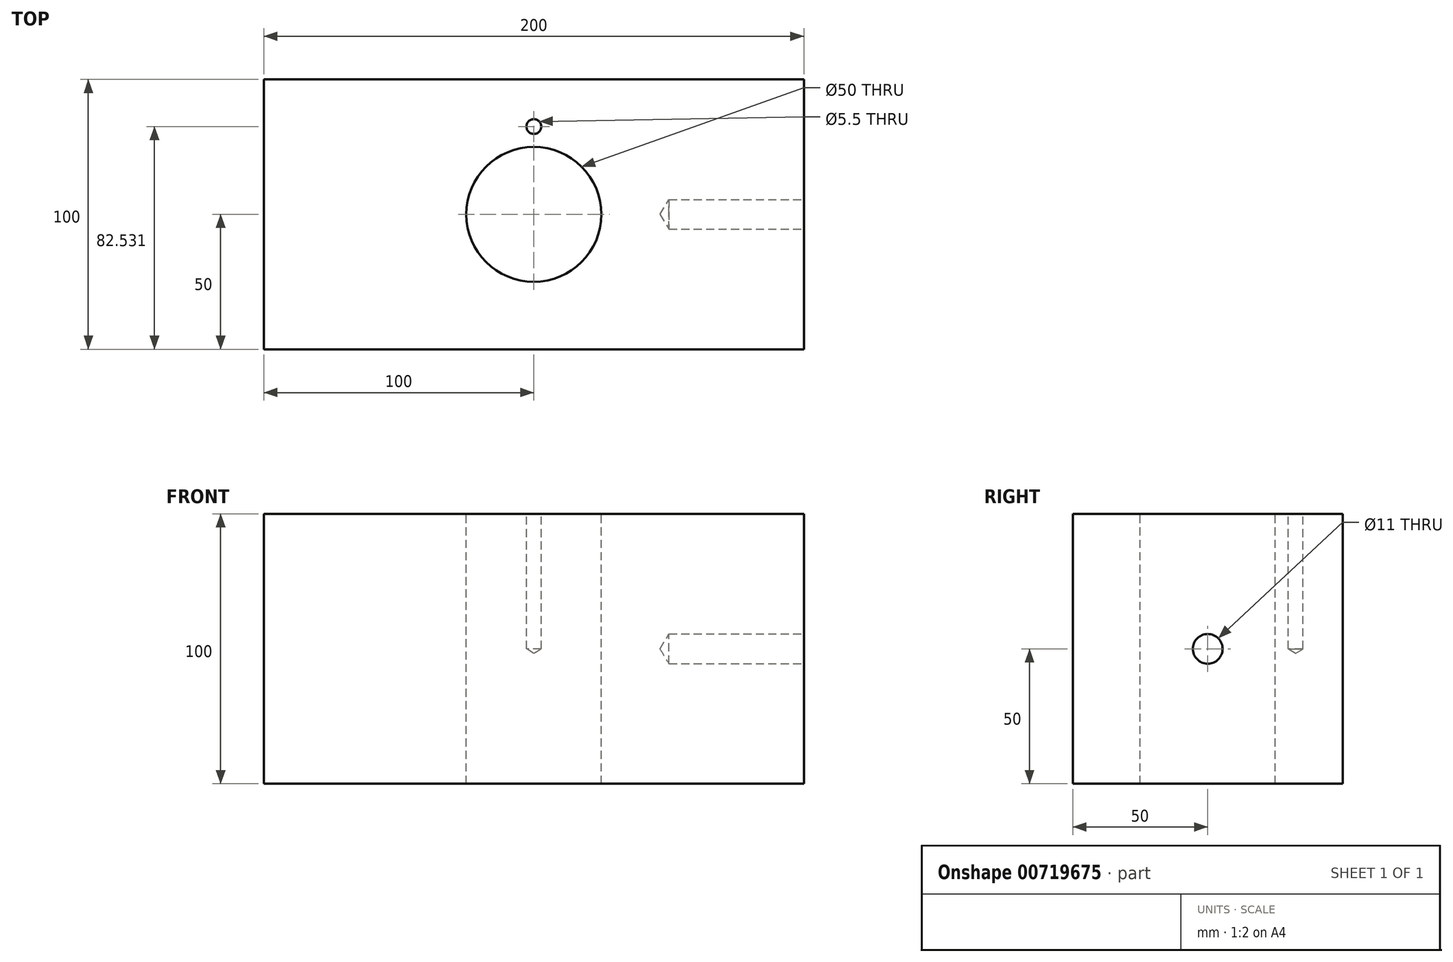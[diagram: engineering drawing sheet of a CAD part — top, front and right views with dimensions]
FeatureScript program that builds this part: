
annotation { "Feature Type Name" : "Feature", "Feature Type Description" : "" }
export const myFeature = defineFeature(function(context is Context, id is Id, definition is map)
    precondition{}
    {
        {
            var Q0;
            Q0=qCreatedBy(makeId("Top.planeOp"),FACE);
            var sketch = newSketch(context, id + "F0", { "sketchPlane" : qUnion([Q0])});
            skLineSegment(sketch, "E0.bottom", {"start": v(100, -50) * mm, "end": v(-100, -50) * mm});
            skLineSegment(sketch, "E0.top", {"start": v(100, 50) * mm, "end": v(-100, 50) * mm});
            skLineSegment(sketch, "E0.left", {"start": v(100, -50) * mm, "end": v(100, 50) * mm});
            skLineSegment(sketch, "E0.right", {"start": v(-100, -50) * mm, "end": v(-100, 50) * mm});
            skPoint(sketch, "E0.middle", {"position": v(0, 0) * mm});
            skSolve(sketch);
        }
        {
            var Q0;
            Q0=makeQuery(id+"F0.imprint","IMPRINT",FACE,{"disambiguationData":[TD([[makeQuery(id+"F0.imprint","IMPRINT",EDGE,{"derivedFrom":sQuery(id+"F0.wireOp",EDGE,"E0.bottom")}),-1.0]])]});
            extrude(context, id + "F1", {"entities" : qUnion([Q0]), "endBound" : BoundingType.SYMMETRIC, "depth" : 100 * mm, "offsetDistance" : 25 * mm});
        }
        {
            var Q0;
            Q0=makeQuery(id+"F1.opExtrude","CAP_FACE",FACE,{"disambiguationData":[OSD([sQuery(id+"F0.wireOp",EDGE,"E0.bottom"),sQuery(id+"F0.wireOp",EDGE,"E0.top"),sQuery(id+"F0.wireOp",EDGE,"E0.left"),sQuery(id+"F0.wireOp",EDGE,"E0.right")])],"isStart":false});
            var sketch = newSketch(context, id + "F2", { "sketchPlane" : qUnion([Q0])});
            skCircle(sketch, "E1", {"center": v(0, 0) * mm, "radius": 25 * mm});
            skSolve(sketch);
        }
        {
            var Q0;
            Q0=makeQuery(id+"F2.imprint","IMPRINT",FACE,{"disambiguationData":[TD([[makeQuery(id+"F2.imprint","IMPRINT",EDGE,{"derivedFrom":sQuery(id+"F2.wireOp",EDGE,"E1")}),1.0]])]});
            extrude(context, id + "F3", {"entities" : qUnion([Q0]), "operationType" : NewBodyOperationType.REMOVE, "endBound" : BoundingType.THROUGH_ALL, "oppositeDirection" : true, "depth" : 25 * mm, "offsetDistance" : 25 * mm});
        }
        {
            var Q0;
            Q0=makeQuery(id+"F1.opExtrude","SWEPT_FACE",FACE,{"disambiguationData":[OSD([sQuery(id+"F0.wireOp",EDGE,"E0.left")])]});
            var sketch = newSketch(context, id + "F4", { "sketchPlane" : qUnion([Q0])});
            skPoint(sketch, "E2", {"position": v(0, 0) * mm});
            skSolve(sketch);
        }
        {
            var Q0;
            Q0=sQuery(id+"F4.wireOp",VERTEX,"E2");
            var Q1;
            Q1=makeQuery(id+"F1.opExtrude","SWEPT_BODY",BODY,{"disambiguationData":[OSD([sQuery(id+"F0.wireOp",EDGE,"E0.bottom"),sQuery(id+"F0.wireOp",EDGE,"E0.top"),sQuery(id+"F0.wireOp",EDGE,"E0.left"),sQuery(id+"F0.wireOp",EDGE,"E0.right")])]});
            hole(context, id + "F5", {"style" : HoleStyle.SIMPLE, "endStyle" : HoleEndStyle.BLIND, "standardTappedOrClearance" : lookupTablePath({ "standard" : "ISO", "fit" : "Normal", "size" : "M10", "type" : "Clearance" }), "standardBlindInLast" : lookupTablePath({ "fit" : "Standard", "standard" : "ISO", "size" : "M10", "type" : "Clearance" }), "holeDiameter" : 11 * mm, "majorDiameter" : 5 * mm, "holeDepth" : 50 * mm, "isTappedThrough" : true, "tappedDepth" : 12 * mm, "tapClearance" : 3, "locations" : qUnion([Q0]), "scope" : qUnion([Q1])});
        }
        {
            var Q0;
            Q0=makeQuery(id+"F1.opExtrude","CAP_FACE",FACE,{"disambiguationData":[OSD([sQuery(id+"F0.wireOp",EDGE,"E0.bottom"),sQuery(id+"F0.wireOp",EDGE,"E0.top"),sQuery(id+"F0.wireOp",EDGE,"E0.left"),sQuery(id+"F0.wireOp",EDGE,"E0.right")])],"isStart":false});
            var sketch = newSketch(context, id + "F6", { "sketchPlane" : qUnion([Q0])});
            skLineSegment(sketch, "E3", {"start": v(0, 0) * mm, "end": v(0, 32.53) * mm});
            skLineSegment(sketch, "E4.1.0", {"start": v(0, 0) * mm, "end": v(-23, 23) * mm, "construction": true});
            skLineSegment(sketch, "E4.2.0", {"start": v(0, 0) * mm, "end": v(-32.53, 0) * mm});
            skLineSegment(sketch, "E4.3.0", {"start": v(0, 0) * mm, "end": v(-23, -23) * mm});
            skLineSegment(sketch, "E4.4.0", {"start": v(0, 0) * mm, "end": v(0, -32.53) * mm});
            skLineSegment(sketch, "E4.5.0", {"start": v(0, 0) * mm, "end": v(23, -23) * mm});
            skLineSegment(sketch, "E4.6.0", {"start": v(0, 0) * mm, "end": v(32.53, 0) * mm});
            skLineSegment(sketch, "E4.7.0", {"start": v(0, 0) * mm, "end": v(23, 23) * mm});
            skPoint(sketch, "E4.center", {"position": v(0, 0) * mm});
            skSolve(sketch);
        }
        {
            var Q0;
            Q0=sQuery(id+"F6.wireOp",VERTEX,"E3.end");
            var Q1;
            Q1=makeQuery(id+"F1.opExtrude","SWEPT_BODY",BODY,{"disambiguationData":[OSD([sQuery(id+"F0.wireOp",EDGE,"E0.bottom"),sQuery(id+"F0.wireOp",EDGE,"E0.top"),sQuery(id+"F0.wireOp",EDGE,"E0.left"),sQuery(id+"F0.wireOp",EDGE,"E0.right")])]});
            hole(context, id + "F7", {"style" : HoleStyle.SIMPLE, "endStyle" : HoleEndStyle.BLIND, "standardTappedOrClearance" : lookupTablePath({ "standard" : "ISO", "fit" : "Normal", "size" : "M5", "type" : "Clearance" }), "standardBlindInLast" : lookupTablePath({ "fit" : "Standard", "standard" : "ISO", "size" : "M5", "type" : "Clearance" }), "holeDiameter" : 5.5 * mm, "majorDiameter" : 5 * mm, "holeDepth" : 50 * mm, "isTappedThrough" : true, "tappedDepth" : 12 * mm, "tapClearance" : 3, "locations" : qUnion([Q0]), "scope" : qUnion([Q1])});
        }
    });
